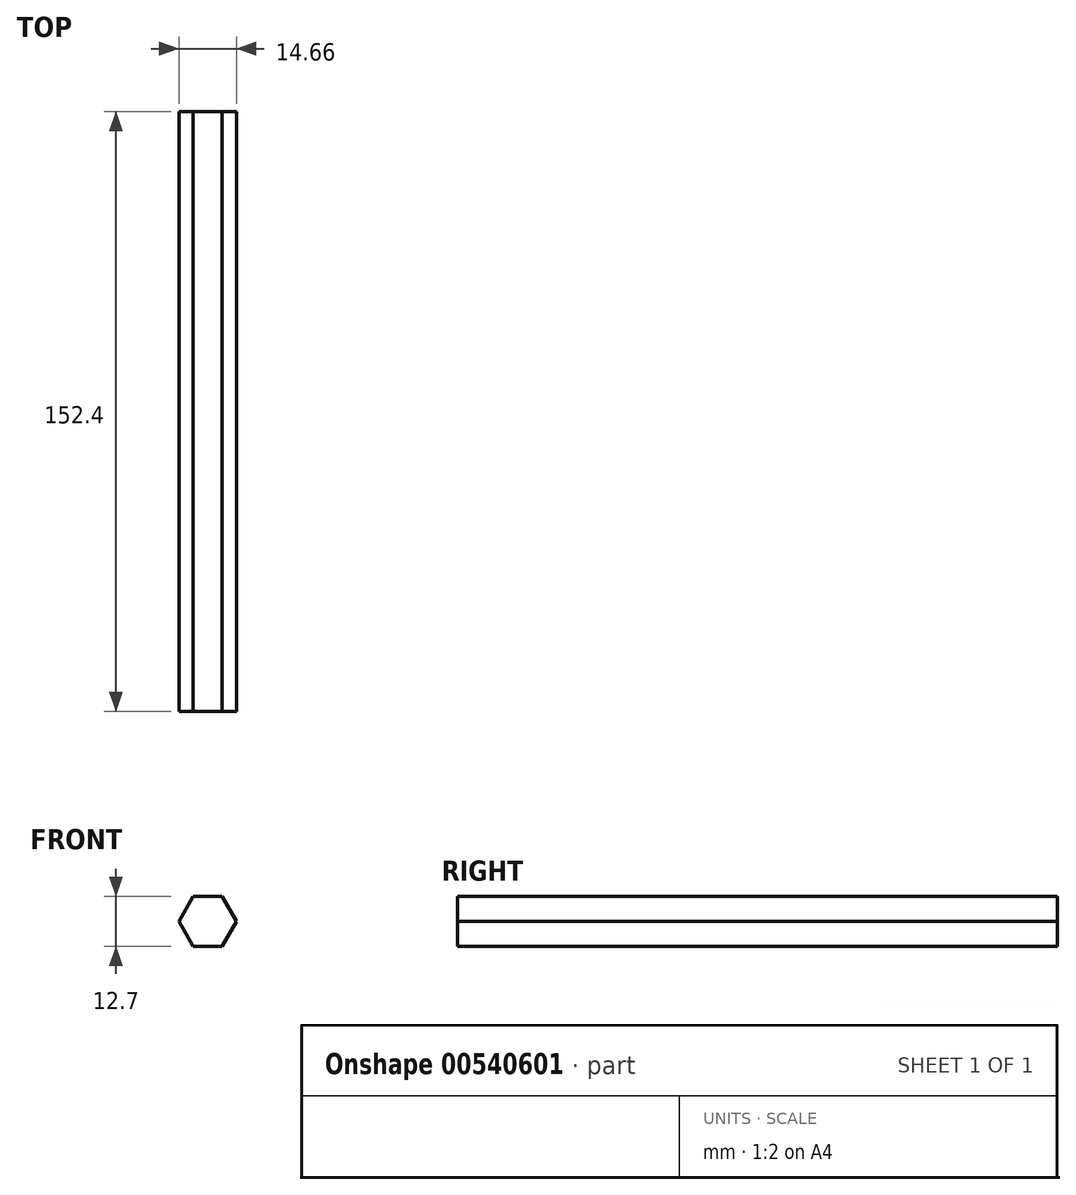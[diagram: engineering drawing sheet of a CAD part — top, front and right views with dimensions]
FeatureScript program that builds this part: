
annotation { "Feature Type Name" : "Feature", "Feature Type Description" : "" }
export const myFeature = defineFeature(function(context is Context, id is Id, definition is map)
    precondition{}
    {
        {
            var Q0;
            Q0=qCreatedBy(makeId("Front.planeOp"),FACE);
            var sketch = newSketch(context, id + "F0", { "sketchPlane" : qUnion([Q0])});
            skCircle(sketch, "E0.cCircle", {"center": v(0, 0) * mm, "radius": 6.35 * mm, "construction": true});
            skLineSegment(sketch, "E0.0", {"start": v(-3.67, 6.35) * mm, "end": v(3.67, 6.35) * mm});
            skLineSegment(sketch, "E0.1", {"start": v(3.67, 6.35) * mm, "end": v(7.33, 0) * mm});
            skLineSegment(sketch, "E0.2", {"start": v(7.33, 0) * mm, "end": v(3.67, -6.35) * mm});
            skLineSegment(sketch, "E0.3", {"start": v(3.67, -6.35) * mm, "end": v(-3.67, -6.35) * mm});
            skLineSegment(sketch, "E0.4", {"start": v(-3.67, -6.35) * mm, "end": v(-7.33, 0) * mm});
            skLineSegment(sketch, "E0.5", {"start": v(-7.33, 0) * mm, "end": v(-3.67, 6.35) * mm});
            skPoint(sketch, "E0.0.midPoint", {"position": v(0, 6.35) * mm});
            skSolve(sketch);
        }
        {
            var Q0;
            Q0=makeQuery(id+"F0.imprint","IMPRINT",FACE,{"disambiguationData":[TD([[makeQuery(id+"F0.imprint","IMPRINT",EDGE,{"derivedFrom":sQuery(id+"F0.wireOp",EDGE,"E0.0")}),-1.0]])]});
            extrude(context, id + "F1", {"entities" : qUnion([Q0]), "depth" : 152.4 * mm, "offsetDistance" : 25.4 * mm});
        }
    });
